# Revit family: 1183xxx Messina 160 II & Messina 160 Frsoted II
name_source: partatom
category: Lighting Fixtures
revit_build: Autodesk Revit 2018 (Build: 20170223_1515(x64)
units: mm (PartAtom-declared; Revit-internal decimal feet)

## family parameters
Always vertical = Yes
Cut with Voids When Loaded = No
Host = Wall
Light Source = No
OmniClass Number = 23.80.70.00
OmniClass Title = Lighting
Part Type = Normal
Room Calculation Point = No
Round Connector Dimension = Use Diameter
Shared = No

## types (6) — shared parameters
Dimmable = Lamp Dependent
Dimming Method = Lamp Dependent
Driver Required = No
Efficacy (lm/w) = Lamp Dependent
Electrical Class = 1
IP rating = 44
Lamp = 1 X E27
Length of Cable Supplied = -
Light Source Fixed = No
Manufacturer = Astro Lighting Ltd
Power (Watts) = 12 Watt LED Max
Product Location = Outdoors
Size MM = 350 x 160 x 100
URL = www.astrolighting.com
Wattage Comments = -
Weight KG = 2.1

## per-type parameters (varying)
| type | Main Finish | Main Material | Product Name | Product SKU | Product URL |
| Astro Messina 160 II - Textured Black | Textured Black | Metal - Steel | Messina 160 II | 1183021 | www.astrolighting.com/1183021 |
| Astro Messina 160 Frosted II - Textured Black | Textured Black | Metal - Steel | Messina 160 Frosted II | 1183024 | www.astrolighting.com/1183024 |
| Astro Messina 160 II - Polished Nickel | Polished Nickel | Metal - Stainless Steel | Messina 160 II | 1183022 | www.astrolighting.com/1183022 |
| Astro Messina 160 Frosted II - Polished Nickel | Polished Nickel | Metal - Stainless Steel | Messina 160 Frosted II | 1183025 | www.astrolighting.com/1183025 |
| Astro Messina 160 Frosted II - Bronze | Bronze | Metal - Stainless Steel | Messina 160 Frosted II | 1183026 | www.astrolighting.com/1183026 |
| Astro Messina 160 II - Bronze | Bronze | Metal - Stainless Steel | Messina 160  II | 1183023 | www.astrolighting.com/1183023 |

## geometry (parser evidence)
native form markers: Sweep x2
no freeform markers — native parametric forms only
